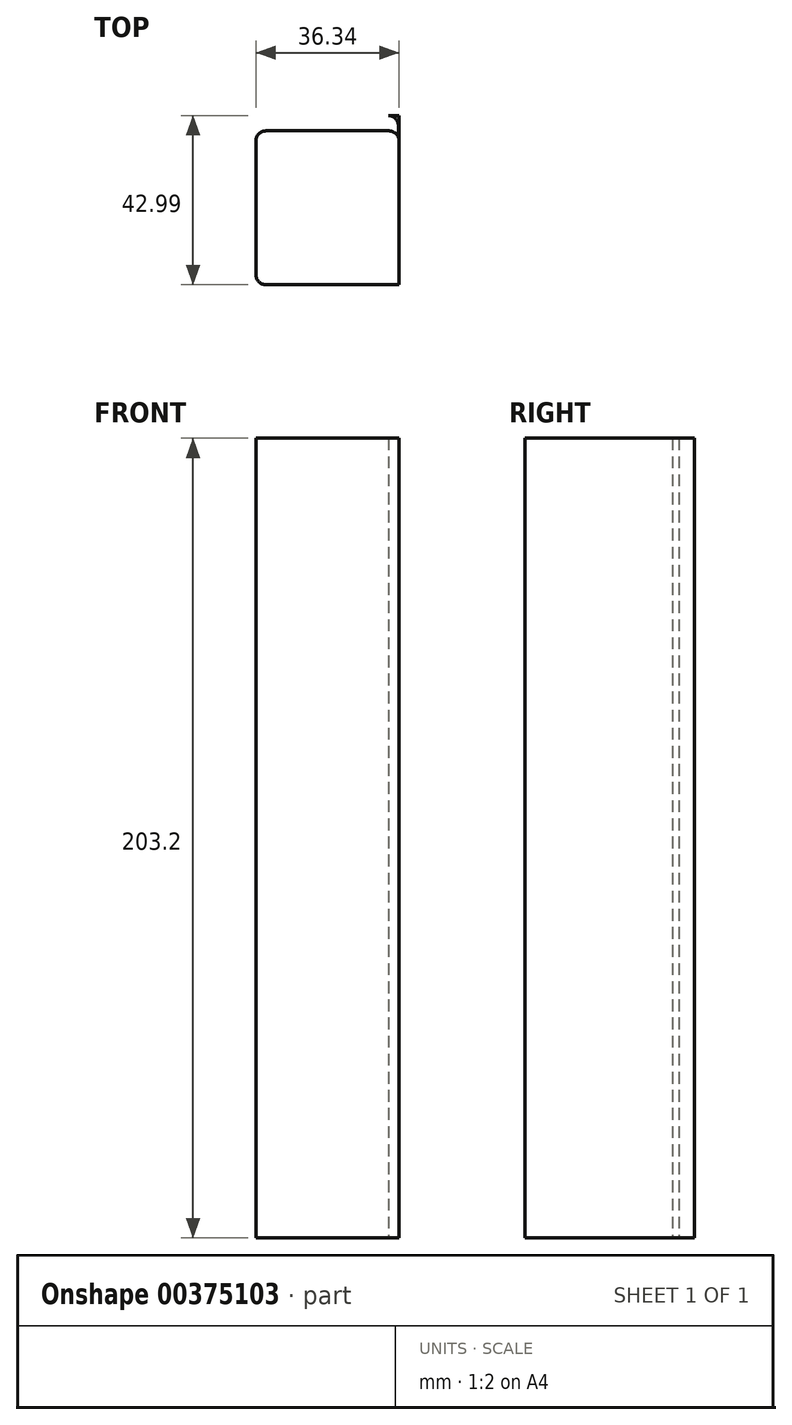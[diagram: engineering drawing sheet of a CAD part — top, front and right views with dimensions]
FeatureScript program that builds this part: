
annotation { "Feature Type Name" : "Feature", "Feature Type Description" : "" }
export const myFeature = defineFeature(function(context is Context, id is Id, definition is map)
    precondition{}
    {
        {
            var Q0;
            Q0=qCreatedBy(makeId("Top.planeOp"),FACE);
            var sketch = newSketch(context, id + "F0", { "sketchPlane" : qUnion([Q0])});
            skLineSegment(sketch, "E0.bottom", {"start": v(-59.41, -15.24) * mm, "end": v(-25.61, -15.24) * mm});
            skLineSegment(sketch, "E0.top", {"start": v(-59.41, 23.85) * mm, "end": v(-28.15, 23.85) * mm});
            skLineSegment(sketch, "E0.left", {"start": v(-61.95, -12.7) * mm, "end": v(-61.95, 21.3) * mm});
            skLineSegment(sketch, "E0.right", {"start": v(-25.61, -15.24) * mm, "end": v(-25.61, 21.3) * mm});
            skLineSegment(sketch, "E1.bottom", {"start": v(-28.3, -15.24) * mm, "end": v(-25.61, -15.24) * mm});
            skLineSegment(sketch, "E1.top", {"start": v(-28.3, 27.75) * mm, "end": v(-25.61, 27.75) * mm});
            skLineSegment(sketch, "E1.left", {"start": v(-25.61, -15.24) * mm, "end": v(-25.61, 27.75) * mm});
            skLineSegment(sketch, "E1.right", {"start": v(-25.77, -12.7) * mm, "end": v(-25.77, 25.21) * mm});
            skPoint(sketch, "E2.visualSharp", {"position": v(-61.95, -15.24) * mm});
            skArc(sketch, "E2.filletArc", {"start": v(-61.95, -12.7) * mm, "mid": v(-61.2, -14.5) * mm, "end": v(-59.41, -15.24) * mm});
            skPoint(sketch, "E3.visualSharp", {"position": v(-25.77, 27.75) * mm});
            skArc(sketch, "E3.filletArc", {"start": v(-25.77, 25.21) * mm, "mid": v(-26.51, 27) * mm, "end": v(-28.3, 27.75) * mm});
            skPoint(sketch, "E4.visualSharp", {"position": v(-25.77, -15.24) * mm});
            skArc(sketch, "E4.filletArc", {"start": v(-28.3, -15.24) * mm, "mid": v(-26.51, -14.5) * mm, "end": v(-25.77, -12.7) * mm});
            skPoint(sketch, "E5.visualSharp", {"position": v(-61.95, 23.85) * mm});
            skArc(sketch, "E5.filletArc", {"start": v(-59.41, 23.85) * mm, "mid": v(-61.2, 23.1) * mm, "end": v(-61.95, 21.3) * mm});
            skPoint(sketch, "E6.visualSharp", {"position": v(-25.61, 23.85) * mm});
            skArc(sketch, "E6.filletArc", {"start": v(-25.61, 21.3) * mm, "mid": v(-26.36, 23.1) * mm, "end": v(-28.15, 23.85) * mm});
            skSolve(sketch);
        }
        {
            var Q0;
            {var subQ2=sQuery(id+"F0.wireOp",EDGE,"E0.bottom");Q0=makeQuery(id+"F0.imprint","IMPRINT",FACE,{"disambiguationData":[TD([[makeQuery(id+"F0.imprint","IMPRINT",EDGE,{"derivedFrom":subQ2}),1.0]])]});}
            extrude(context, id + "F1", {"entities" : qUnion([Q0]), "depth" : 203.2 * mm});
        }
        {
            var Q0;
            Q0 = qSketchRegion(id + "F0", true);
            extrude(context, id + "F2", {"entities" : qUnion([Q0]), "operationType" : NewBodyOperationType.ADD, "depth" : 203.2 * mm});
        }
    });
